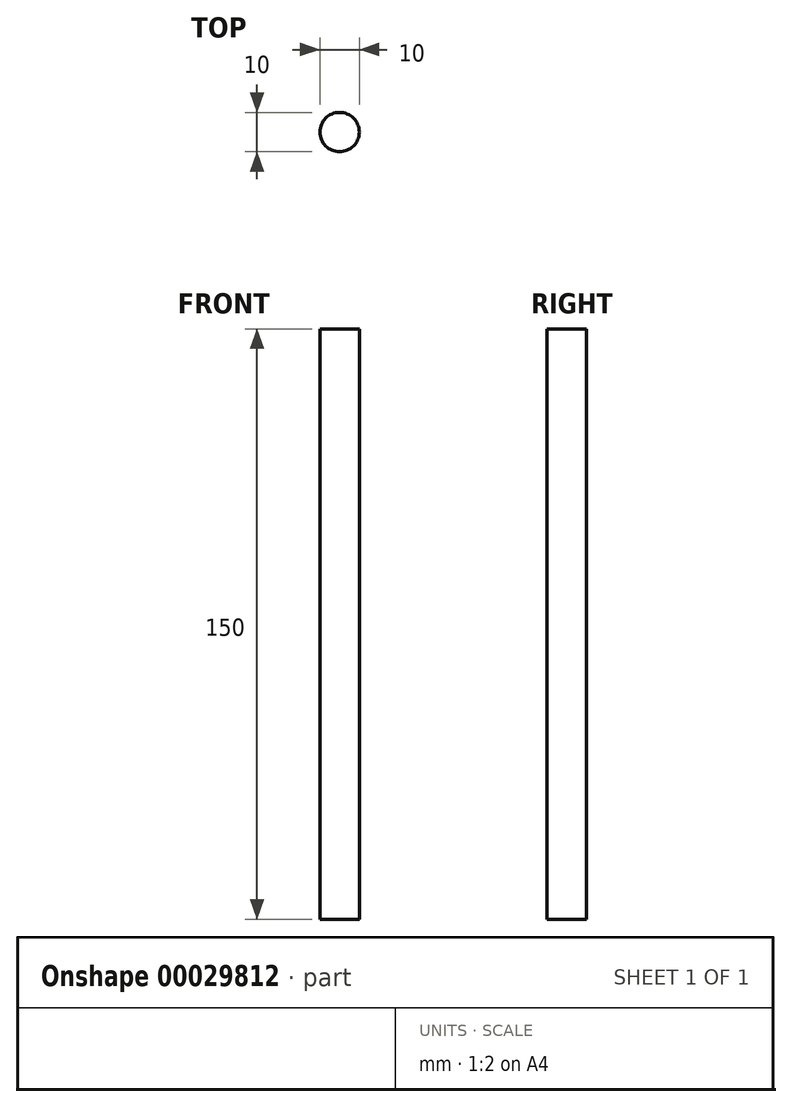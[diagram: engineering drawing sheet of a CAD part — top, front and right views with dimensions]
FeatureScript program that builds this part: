
annotation { "Feature Type Name" : "Feature", "Feature Type Description" : "" }
export const myFeature = defineFeature(function(context is Context, id is Id, definition is map)
    precondition{}
    {
        {
            var Q0;
            Q0=qCreatedBy(makeId("Top.planeOp"),FACE);
            var sketch = newSketch(context, id + "F0", { "sketchPlane" : qUnion([Q0])});
            skCircle(sketch, "E0", {"center": v(0, 0) * mm, "radius": 5 * mm});
            skSolve(sketch);
        }
        {
            var Q0;
            Q0 = qSketchRegion(id + "F0", true);
            extrude(context, id + "F1", {"entities" : qUnion([Q0]), "endBound" : BoundingType.SYMMETRIC, "depth" : 150 * mm});
        }
    });
